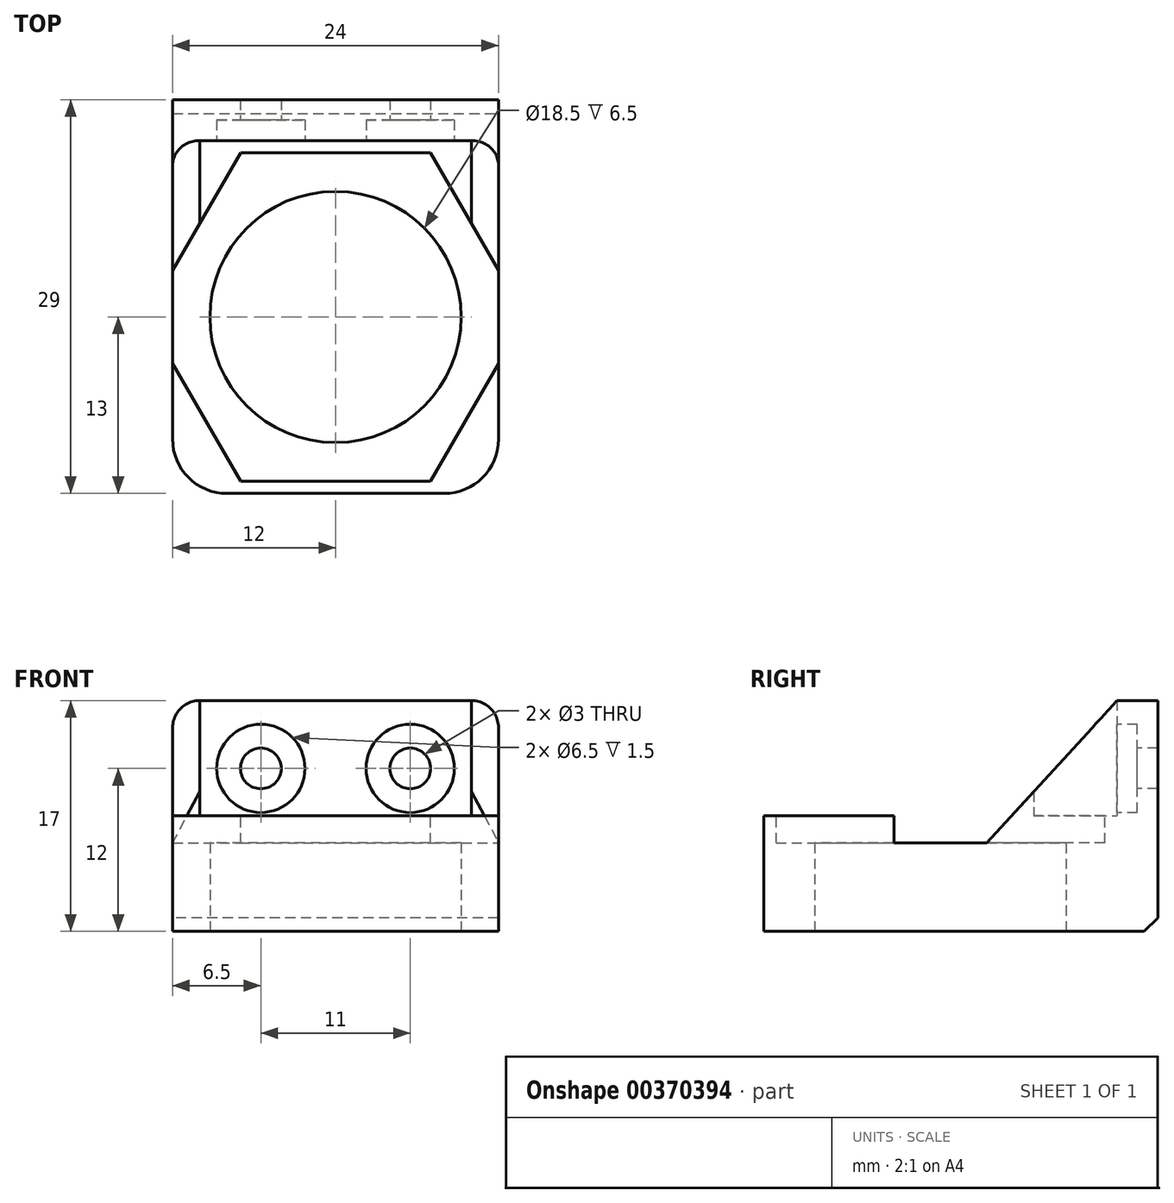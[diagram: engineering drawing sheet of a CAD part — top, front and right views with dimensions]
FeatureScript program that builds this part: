
annotation { "Feature Type Name" : "Feature", "Feature Type Description" : "" }
export const myFeature = defineFeature(function(context is Context, id is Id, definition is map)
    precondition{}
    {
        {
            var Q0;
            Q0=qCreatedBy(makeId("Front.planeOp"),FACE);
            var sketch = newSketch(context, id + "F0", { "sketchPlane" : qUnion([Q0])});
            skLineSegment(sketch, "E0.bottom", {"start": v(24, 12) * mm, "end": v(0, 12) * mm});
            skLineSegment(sketch, "E0.top", {"start": v(24, 0) * mm, "end": v(0, 0) * mm});
            skLineSegment(sketch, "E0.left", {"start": v(24, 12) * mm, "end": v(24, 0) * mm});
            skLineSegment(sketch, "E0.right", {"start": v(0, 12) * mm, "end": v(0, 0) * mm});
            skSolve(sketch);
        }
        {
            var Q0;
            Q0=makeQuery(id+"F0.imprint","IMPRINT",FACE,{"disambiguationData":[TD([[makeQuery(id+"F0.imprint","IMPRINT",EDGE,{"derivedFrom":sQuery(id+"F0.wireOp",EDGE,"E0.bottom")}),1.0]])]});
            extrude(context, id + "F1", {"entities" : qUnion([Q0]), "depth" : 3 * mm, "offsetDistance" : 25 * mm});
        }
        {
            var Q0;
            Q0=makeQuery(id+"F1.opExtrude","CAP_FACE",FACE,{"disambiguationData":[OSD([sQuery(id+"F0.wireOp",EDGE,"E0.bottom"),sQuery(id+"F0.wireOp",EDGE,"E0.top"),sQuery(id+"F0.wireOp",EDGE,"E0.left"),sQuery(id+"F0.wireOp",EDGE,"E0.right")])],"isStart":false});
            var sketch = newSketch(context, id + "F2", { "sketchPlane" : qUnion([Q0])});
            skLineSegment(sketch, "E1.bottom", {"start": v(0, 0) * mm, "end": v(24, 0) * mm});
            skLineSegment(sketch, "E1.top", {"start": v(0, 3.5) * mm, "end": v(24, 3.5) * mm});
            skLineSegment(sketch, "E1.left", {"start": v(0, 0) * mm, "end": v(0, 3.5) * mm});
            skLineSegment(sketch, "E1.right", {"start": v(24, 0) * mm, "end": v(24, 3.5) * mm});
            skLineSegment(sketch, "E2", {"start": v(0, 7) * mm, "end": v(24, 7) * mm, "construction": true});
            skLineSegment(sketch, "E3", {"start": v(17.5, 0) * mm, "end": v(17.5, 12) * mm, "construction": true});
            skLineSegment(sketch, "E4", {"start": v(6.5, 0) * mm, "end": v(6.5, 12) * mm, "construction": true});
            skPoint(sketch, "E5", {"position": v(6.5, 7) * mm});
            skPoint(sketch, "E6", {"position": v(17.5, 7) * mm});
            skCircle(sketch, "E7", {"center": v(6.5, 7) * mm, "radius": 2.5 * mm});
            skLineSegment(sketch, "E8", {"start": v(0, 6) * mm, "end": v(24, 6) * mm, "construction": true});
            skLineSegment(sketch, "E9", {"start": v(12, 12) * mm, "end": v(12, 0) * mm, "construction": true});
            skCircle(sketch, "E10.MirrorC", {"center": v(17.5, 7) * mm, "radius": 2.5 * mm});
            skLineSegment(sketch, "E11.bottom", {"start": v(0, 12) * mm, "end": v(2, 12) * mm});
            skLineSegment(sketch, "E11.top", {"start": v(0, 3.5) * mm, "end": v(2, 3.5) * mm});
            skLineSegment(sketch, "E11.left", {"start": v(0, 12) * mm, "end": v(0, 3.5) * mm});
            skLineSegment(sketch, "E11.right", {"start": v(2, 12) * mm, "end": v(2, 3.5) * mm});
            skLineSegment(sketch, "E12.MirrorCS", {"start": v(22, 12) * mm, "end": v(22, 3.5) * mm});
            skLineSegment(sketch, "E13.MirrorCS", {"start": v(24, 12) * mm, "end": v(22, 12) * mm});
            skLineSegment(sketch, "E14.MirrorCS", {"start": v(24, 12) * mm, "end": v(24, 3.5) * mm});
            skSolve(sketch);
        }
        {
            var Q0;
            Q0=sQuery(id+"F2.wireOp",VERTEX,"E5");
            var Q1;
            Q1=sQuery(id+"F2.wireOp",VERTEX,"E6");
            var Q2;
            Q2=sQuery(id+"F2.wireOp",VERTEX,"9b93672e-2990-476f-b0a9-77059a06add8");
            var Q3;
            Q3=sQuery(id+"F2.wireOp",VERTEX,"ac4e0633-efb0-4ba2-bce2-8fe4dab348f1");
            var Q4;
            Q4=makeQuery(id+"F1.opExtrude","SWEPT_BODY",BODY,{"disambiguationData":[OSD([sQuery(id+"F0.wireOp",EDGE,"E0.bottom"),sQuery(id+"F0.wireOp",EDGE,"E0.top"),sQuery(id+"F0.wireOp",EDGE,"E0.left"),sQuery(id+"F0.wireOp",EDGE,"E0.right")])]});
            hole(context, id + "F3", {"style" : HoleStyle.C_BORE, "endStyle" : HoleEndStyle.THROUGH, "holeDiameter" : 3 * mm, "cBoreDiameter" : 6.5 * mm, "cBoreDepth" : 1.5 * mm, "isTappedThrough" : true, "tappedDepth" : 12 * mm, "tapClearance" : 3, "locations" : qUnion([Q0, Q1, Q2, Q3]), "scope" : qUnion([Q4])});
        }
        {
            var Q0;
            Q0=makeQuery(id+"F2.imprint","IMPRINT",FACE,{"disambiguationData":[TD([[makeQuery(id+"F2.imprint","IMPRINT",EDGE,{"derivedFrom":sQuery(id+"F2.wireOp",EDGE,"E1.bottom")}),-1.0]])]});
            extrude(context, id + "F4", {"entities" : qUnion([Q0]), "operationType" : NewBodyOperationType.ADD, "depth" : 26 * mm, "offsetDistance" : 25 * mm});
        }
        {
            var Q0;
            {var subQ1=sQuery(id+"F2.wireOp",EDGE,"E1.top");Q0=makeQuery(id+"F2.imprint","IMPRINT",FACE,{"disambiguationData":[TD([[makeQuery(id+"F2.imprint","IMPRINT",EDGE,{"derivedFrom":subQ1}),1.0]])]});}
            var sketch = newSketch(context, id + "F5", { "sketchPlane" : qUnion([Q0])});
            skSolve(sketch);
        }
        {
            var Q0;
            Q0=makeQuery(id+"F4.opExtrude","SWEPT_FACE",FACE,{"disambiguationData":[OSD([sQuery(id+"F2.wireOp",EDGE,"E1.top")])]});
            var sketch = newSketch(context, id + "F6", { "sketchPlane" : qUnion([Q0])});
            skCircle(sketch, "E15.cCircle", {"center": v(12, -16) * mm, "radius": 12.1 * mm, "construction": true});
            skLineSegment(sketch, "E15.0", {"start": v(5.01, -28.1) * mm, "end": v(-1.97, -16) * mm});
            skLineSegment(sketch, "E15.1", {"start": v(-1.97, -16) * mm, "end": v(5.01, -3.9) * mm});
            skLineSegment(sketch, "E15.2", {"start": v(5.01, -3.9) * mm, "end": v(18.99, -3.9) * mm});
            skLineSegment(sketch, "E15.3", {"start": v(18.99, -3.9) * mm, "end": v(25.97, -16) * mm});
            skLineSegment(sketch, "E15.4", {"start": v(25.97, -16) * mm, "end": v(18.99, -28.1) * mm});
            skLineSegment(sketch, "E15.5", {"start": v(18.99, -28.1) * mm, "end": v(5.01, -28.1) * mm});
            skLineSegment(sketch, "E16", {"start": v(12, -29) * mm, "end": v(12, -3) * mm, "construction": true});
            skSolve(sketch);
        }
        {
            var Q0;
            Q0=makeQuery(id+"F4.opExtrude","CAP_EDGE",EDGE,{"disambiguationData":[OSD([sQuery(id+"F2.wireOp",EDGE,"E1.right")])],"isStart":false});
            var Q1;
            Q1=makeQuery(id+"F5kRuORAZ8C9X0k_1.boolean.opBoolean","COPY",EDGE,{"derivedFrom":makeQuery(id+"F5kRuORAZ8C9X0k_1.opExtrude","SWEPT_EDGE",EDGE,{"disambiguationData":[OSD([sQuery(id+"F2.wireOp",EDGE,"E1.bottom"),sQuery(id+"F8.wireOp",EDGE,"GbdEAWLs-SJBU-rbzc-2olr-KBSKZh6psz5a")])]})});
            var Q2;
            Q2=makeQuery(id+"F5kRuORAZ8C9X0k_1.boolean.opBoolean","COPY",EDGE,{"derivedFrom":makeQuery(id+"F5kRuORAZ8C9X0k_1.opExtrude","SWEPT_EDGE",EDGE,{"disambiguationData":[OSD([sQuery(id+"F2.wireOp",EDGE,"E1.bottom"),sQuery(id+"F8.wireOp",EDGE,"kYlhJU9l-gKN5-24du-RjB6-uRuuNHYteBA4")])]})});
            var Q3;
            Q3=makeQuery(id+"F4.opExtrude","CAP_EDGE",EDGE,{"disambiguationData":[OSD([sQuery(id+"F2.wireOp",EDGE,"E1.left")])],"isStart":false});
            fillet(context, id + "F7", {"entities" : qUnion([Q0, Q1, Q2, Q3]), "radius" : 4 * mm, "tangentPropagation" : true, "allowEdgeOverflow" : false});
        }
        {
            var Q0;
            Q0=makeQuery(id+"F4.opExtrude","SWEPT_FACE",FACE,{"disambiguationData":[OSD([sQuery(id+"F2.wireOp",EDGE,"E1.bottom")])]});
            var sketch = newSketch(context, id + "F8", { "sketchPlane" : qUnion([Q0])});
            skLineSegment(sketch, "E17", {"start": v(12, 30.73) * mm, "end": v(12, 29) * mm, "construction": true});
            skCircle(sketch, "E18", {"center": v(12, 16) * mm, "radius": 9.25 * mm});
            skPoint(sketch, "E19", {"position": v(12, 0) * mm});
            skLineSegment(sketch, "E20", {"start": v(0, 17) * mm, "end": v(24, 17) * mm, "construction": true});
            skSolve(sketch);
        }
        {
            var Q0;
            Q0=makeQuery(id+"F8.imprint","IMPRINT",FACE,{"disambiguationData":[TD([[makeQuery(id+"F8.imprint","IMPRINT",EDGE,{"derivedFrom":sQuery(id+"F8.wireOp",EDGE,"E18")}),1.0]])]});
            extrude(context, id + "F9", {"entities" : qUnion([Q0]), "operationType" : NewBodyOperationType.REMOVE, "oppositeDirection" : true, "depth" : 25 * mm});
        }
        {
            var Q0;
            Q0=makeQuery(id+"F4.boolean.opBoolean","MERGE",FACE,{"derivedFrom":[makeQuery(id+"F1.opExtrude","SWEPT_FACE",FACE,{"disambiguationData":[OSD([sQuery(id+"F0.wireOp",EDGE,"E0.top")])]}),makeQuery(id+"F4.opExtrude","SWEPT_FACE",FACE,{"disambiguationData":[OSD([sQuery(id+"F2.wireOp",EDGE,"E1.bottom")])]})]});
            extrude(context, id + "F10", {"entities" : qUnion([Q0]), "operationType" : NewBodyOperationType.ADD, "depth" : 5 * mm});
        }
        {
            var Q0;
            {var subQ7=sQuery(id+"F6.wireOp",EDGE,"E15.2");var subQ8=sQuery(id+"F6.wireOp",EDGE,"E15.1");var subQ9=makeQuery(id+"F6.imprint","INTERSECT",VERTEX,{"derivedFrom":[subQ8,subQ7]});Q0=makeQuery(id+"F6.imprint","IMPRINT",FACE,{"disambiguationData":[TD([[makeQuery(id+"F6.imprint","IMPRINT",EDGE,{"disambiguationData":[TD([[subQ9,1.0]])],"derivedFrom":subQ8}),-1.0]])]});}
            extrude(context, id + "F11", {"entities" : qUnion([Q0]), "operationType" : NewBodyOperationType.REMOVE, "oppositeDirection" : true, "depth" : 2 * mm});
        }
        {
            var Q0;
            Q0=makeQuery(id+"F2.imprint","IMPRINT",FACE,{"disambiguationData":[TD([[makeQuery(id+"F2.imprint","IMPRINT",EDGE,{"derivedFrom":sQuery(id+"F2.wireOp",EDGE,"E11.bottom")}),1.0]])]});
            var Q1;
            Q1=makeQuery(id+"F11.boolean.opBoolean","COPY",FACE,{"derivedFrom":makeQuery(id+"F11.opExtrude","SWEPT_FACE",FACE,{"disambiguationData":[OSD([sQuery(id+"F6.wireOp",EDGE,"E15.1")])]})});
            var Q2;
            Q2=makeQuery(id+"F1.opExtrude","SWEPT_BODY",BODY,{"disambiguationData":[OSD([sQuery(id+"F0.wireOp",EDGE,"E0.bottom"),sQuery(id+"F0.wireOp",EDGE,"E0.top"),sQuery(id+"F0.wireOp",EDGE,"E0.left"),sQuery(id+"F0.wireOp",EDGE,"E0.right")])]});
            var Q3;
            Q3=sQuery(id+"F6.wireOp",VERTEX,"E15.4.start");
            extrude(context, id + "F12", {"entities" : qUnion([Q0]), "operationType" : NewBodyOperationType.ADD, "endBound" : BoundingType.UP_TO_SURFACE, "endBoundEntityFace" : qUnion([Q1]), "endBoundEntityBody" : qUnion([Q2]), "endBoundEntityVertex" : qUnion([Q3]), "depth" : 5 * mm, "offsetDistance" : 25 * mm});
        }
        {
            var Q0;
            {var subQ2=sQuery(id+"F2.wireOp",EDGE,"E12.MirrorCS");Q0=makeQuery(id+"F5.imprint","IMPRINT",FACE,{"disambiguationData":[TD([[makeQuery(id+"F5.imprint","IMPRINT",EDGE,{"derivedFrom":makeQuery(id+"F2.imprint","IMPRINT",EDGE,{"derivedFrom":subQ2})}),1.0]])]});}
            var Q1;
            Q1=makeQuery(id+"F11.boolean.opBoolean","COPY",FACE,{"derivedFrom":makeQuery(id+"F11.opExtrude","SWEPT_FACE",FACE,{"disambiguationData":[OSD([sQuery(id+"F6.wireOp",EDGE,"E15.3")])]})});
            extrude(context, id + "F13", {"entities" : qUnion([Q0]), "operationType" : NewBodyOperationType.ADD, "endBound" : BoundingType.UP_TO_SURFACE, "endBoundEntityFace" : qUnion([Q1]), "depth" : 25 * mm, "offsetDistance" : 25 * mm});
        }
        {
            var Q0;
            Q0=makeQuery(id+"F10.opExtrude","CAP_EDGE",EDGE,{"disambiguationData":[OSD([sQuery(id+"F0.wireOp",EDGE,"E0.top")])],"isStart":false});
            chamfer(context, id + "F14", {"entities" : qUnion([Q0]), "width" : 1 * mm, "tangentPropagation" : true});
        }
        {
            var Q0;
            Q0=makeQuery(id+"F1.opExtrude","SWEPT_EDGE",EDGE,{"disambiguationData":[OSD([sQuery(id+"F0.wireOp",EDGE,"E0.bottom"),sQuery(id+"F0.wireOp",EDGE,"E0.left")])]});
            var Q1;
            Q1=makeQuery(id+"F1.opExtrude","SWEPT_EDGE",EDGE,{"disambiguationData":[OSD([sQuery(id+"F0.wireOp",EDGE,"E0.bottom"),sQuery(id+"F0.wireOp",EDGE,"E0.right")])]});
            fillet(context, id + "F15", {"entities" : qUnion([Q0, Q1]), "radius" : 2 * mm, "tangentPropagation" : true, "allowEdgeOverflow" : false});
        }
        {
            var Q0;
            {var subQ0=sQuery(id+"F2.wireOp",EDGE,"E1.right");var subQ1=sQuery(id+"F0.wireOp",EDGE,"E0.left");Q0=makeQuery(id+"F13.boolean.opBoolean","MERGE",FACE,{"derivedFrom":[makeQuery(id+"F10.boolean.opBoolean","MERGE",FACE,{"derivedFrom":[makeQuery(id+"F4.boolean.opBoolean","MERGE",FACE,{"derivedFrom":[makeQuery(id+"F1.opExtrude","SWEPT_FACE",FACE,{"disambiguationData":[OSD([subQ1])]}),makeQuery(id+"F4.opExtrude","SWEPT_FACE",FACE,{"disambiguationData":[OSD([subQ0])]})]}),makeQuery(id+"F10.opExtrude","SWEPT_FACE",FACE,{"disambiguationData":[OSD([sQuery(id+"F0.wireOp",EDGE,"E0.top"),subQ1,sQuery(id+"F2.wireOp",EDGE,"E1.bottom"),subQ0])]})]}),makeQuery(id+"F13.opExtrude","SWEPT_FACE",FACE,{"disambiguationData":[OSD([sQuery(id+"F2.wireOp",EDGE,"E14.MirrorCS")])]})]});}
            var sketch = newSketch(context, id + "F16", { "sketchPlane" : qUnion([Q0])});
            skLineSegment(sketch, "E21", {"start": v(-12.58, 1.5) * mm, "end": v(-3, 12) * mm});
            skLineSegment(sketch, "E22", {"start": v(-3, 12) * mm, "end": v(-12.58, 12) * mm});
            skLineSegment(sketch, "E23", {"start": v(-12.58, 12) * mm, "end": v(-12.58, 1.5) * mm});
            skSolve(sketch);
        }
        {
            var Q0;
            Q0=qSketchRegion(id+"F16",true);
            extrude(context, id + "F17", {"entities" : qUnion([Q0]), "operationType" : NewBodyOperationType.REMOVE, "oppositeDirection" : true, "depth" : 25 * mm, "offsetDistance" : 25 * mm});
        }
    });
